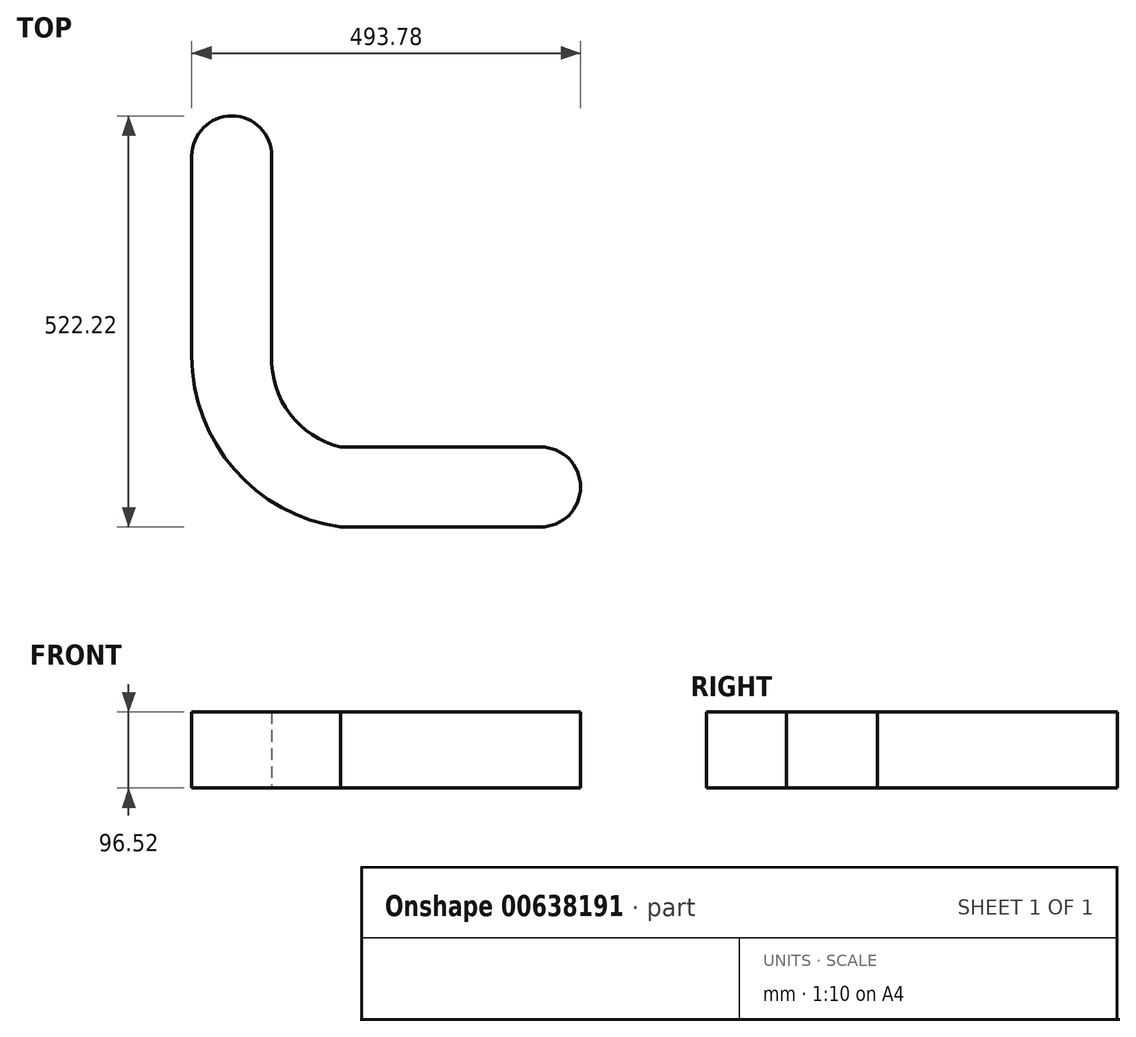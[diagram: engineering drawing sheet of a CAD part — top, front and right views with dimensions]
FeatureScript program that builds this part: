
annotation { "Feature Type Name" : "Feature", "Feature Type Description" : "" }
export const myFeature = defineFeature(function(context is Context, id is Id, definition is map)
    precondition{}
    {
        {
            var Q0;
            Q0=qCreatedBy(makeId("Top.planeOp"),FACE);
            var sketch = newSketch(context, id + "F0", { "sketchPlane" : qUnion([Q0])});
            skLineSegment(sketch, "E0", {"start": v(-721.36, 0) * mm, "end": v(-721.36, 254) * mm});
            skLineSegment(sketch, "E1", {"start": v(-619.76, 254) * mm, "end": v(-619.76, 0) * mm});
            skArc(sketch, "E2", {"start": v(-619.76, 254) * mm, "mid": v(-670.56, 304.8) * mm, "end": v(-721.36, 254) * mm});
            skArc(sketch, "E3", {"start": v(-619.76, 0) * mm, "mid": v(-596.83, -73.57) * mm, "end": v(-532.38, -115.82) * mm});
            skLineSegment(sketch, "E4", {"start": v(-532.38, -115.82) * mm, "end": v(-278.38, -115.82) * mm});
            skLineSegment(sketch, "E5", {"start": v(-278.38, -217.42) * mm, "end": v(-532.38, -217.42) * mm});
            skArc(sketch, "E6", {"start": v(-721.36, 0) * mm, "mid": v(-667.51, -144.04) * mm, "end": v(-532.38, -217.42) * mm});
            skArc(sketch, "E7", {"start": v(-278.38, -217.42) * mm, "mid": v(-227.58, -166.62) * mm, "end": v(-278.38, -115.82) * mm});
            skSolve(sketch);
        }
        {
            var Q0;
            Q0=makeQuery(id+"F0.imprint","IMPRINT",FACE,{"disambiguationData":[TD([[makeQuery(id+"F0.imprint","IMPRINT",EDGE,{"derivedFrom":sQuery(id+"F0.wireOp",EDGE,"E0")}),-1.0]])]});
            extrude(context, id + "F1", {"entities" : qUnion([Q0]), "depth" : 96.52 * mm, "offsetDistance" : 25.4 * mm});
        }
    });
